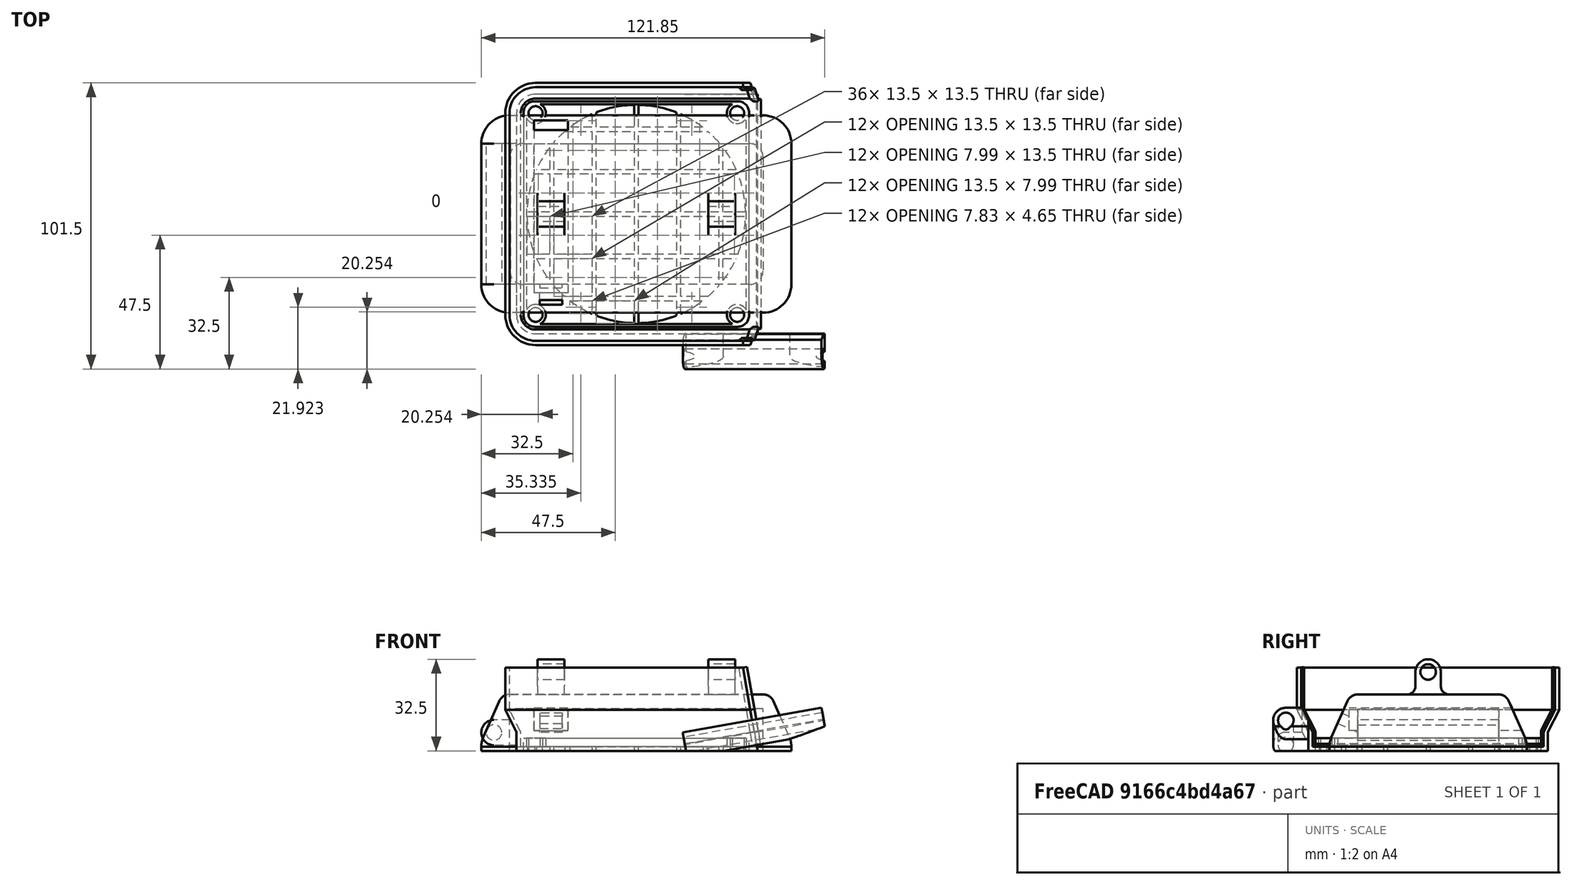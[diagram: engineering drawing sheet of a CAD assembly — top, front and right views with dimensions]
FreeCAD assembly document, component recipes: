
FREECAD ASSEMBLY — COMPONENT RECIPES ("Solder Fume Extractor 2x80mm fans - v2")

This assembly document has 5 components, labeled P0..P4 below (a component is one placed body or linked part). 5 of them carry a construction recipe — the FreeCAD feature program that regenerates the part from scratch, quoted from this document or its linked companion documents; the rest are supplied as boundary geometry only. No exploded tour is included for this assembly.
COMPONENT P0 — recipe-attached ("Fan1Holder", modeled in this document).
Construction recipe (the document's own serialized feature program — sketch geometry with constraints, then the solid features built on it; lengths are millimeters unless a unit is written):

FEATURE [Sketcher::SketchObject] Sketch
  ArcFitTolerance = 1e-06
  AttachmentSupport = -> [XY_Plane]
  FullyConstrained = true
  MakeInternals = false
  MapMode = 5
  sketch-geometry (13):
    g0: LineSegment StartX=-42.5 StartY=35.75 StartZ=0 EndX=-42.5 EndY=-35.75 EndZ=0
    g1: LineSegment StartX=-35.75 StartY=-42.5 StartZ=0 EndX=60 EndY=-42.5 EndZ=0
    g2: LineSegment StartX=60 StartY=-42.5 StartZ=0 EndX=60 EndY=42.5 EndZ=0
    g3: LineSegment StartX=60 StartY=42.5 StartZ=0 EndX=-35.75 EndY=42.5 EndZ=0
    g4: Circle CenterX=-35.75 CenterY=35.75 CenterZ=0 NormalX=0 NormalY=0 NormalZ=1 AngleXU=0 Radius=2.5
    g5: Circle CenterX=35.75 CenterY=35.75 CenterZ=0 NormalX=0 NormalY=0 NormalZ=1 AngleXU=0 Radius=2.5
    g6: Circle CenterX=-35.75 CenterY=-35.75 CenterZ=0 NormalX=0 NormalY=0 NormalZ=1 AngleXU=0 Radius=2.5
    g7: Circle CenterX=35.75 CenterY=-35.75 CenterZ=0 NormalX=0 NormalY=0 NormalZ=1 AngleXU=0 Radius=2.5
    g8: Circle CenterX=0 CenterY=0 CenterZ=0 NormalX=0 NormalY=0 NormalZ=1 AngleXU=0 Radius=38.75
    g9: ArcOfCircle CenterX=-35.75 CenterY=35.75 CenterZ=0 NormalX=0 NormalY=0 NormalZ=1 AngleXU=0 Radius=6.75 StartAngle=1.5708 EndAngle=3.14159
    g10: GeomPoint [constr] X=-42.5 Y=42.5 Z=0
    g11: ArcOfCircle CenterX=-35.75 CenterY=-35.75 CenterZ=0 NormalX=0 NormalY=0 NormalZ=1 AngleXU=0 Radius=6.75 StartAngle=3.14159 EndAngle=4.71239
    g12: GeomPoint [constr] X=-42.5 Y=-42.5 Z=0
  constraints (30):
    c: Coincident(g1,g2)
    c: Coincident(g2,g3)
    c: Vertical(g2)
    c: Horizontal(g1)
    c: Horizontal(g3)
    c: DistanceY(g12,g10) = 85
    c: Equal(g7,g5)
    c: Equal(g5,g4)
    c: Equal(g4,g6)
    c: Diameter(g7) = 5
    c: Symmetric(g7,g5,g-1)
    c: Symmetric(g5,g4,g-2)
    c: Vertical(g6,g4)
    c: Horizontal(g6,g7)
    c: DistanceX(g4,g5) = 71.5
    c: DistanceY(g6,g4) = 71.5
    c: Symmetric(g12,g10,g-1)
    c: Coincident(g8,g-1)
    c: Diameter(g8) = 77.5
    c: DistanceX(g10,g-1) = 42.5
    c: DistanceX(g1) = 60
    c: PointOnObject(g10,g0)
    c: PointOnObject(g10,g3)
    c: Tangent(g0,g9) = -1.5708
    c: Tangent(g3,g9) = -1.5708
    c: PointOnObject(g12,g1)
    c: Tangent(g0,g11) = -1.5708
    c: Tangent(g1,g11) = -1.5708
    c: Equal(g11,g9)
    c: Coincident(g9,g4)
FEATURE [PartDesign::Pad] Pad
  Direction = (0,0,1)
  Length = 1.5
  Length2 = 10
  Profile = -> Sketch
  ReferenceAxis = -> Sketch [N_Axis]
  Refine = true
  Suppressed = false
  Type = 0
FEATURE [Sketcher::SketchObject] Sketch001
  ArcFitTolerance = 1e-06
  AttachmentSupport = -> [Pad]
  ExternalGeometry = -> [Pad]
  FullyConstrained = true
  MakeInternals = false
  MapMode = 5
  Placement = pos=(0,0,1.5) rot=(0,0,1;0rad)
  sketch-geometry (12):
    g0: LineSegment StartX=60 StartY=42.5 StartZ=0 EndX=-35.75 EndY=42.5 EndZ=0
    g1: LineSegment StartX=-42.5 StartY=35.75 StartZ=0 EndX=-42.5 EndY=-35.75 EndZ=0
    g2: LineSegment StartX=-35.75 StartY=-42.5 StartZ=0 EndX=60 EndY=-42.5 EndZ=0
    g3: ArcOfCircle CenterX=-35.75 CenterY=-35.75 CenterZ=0 NormalX=0 NormalY=0 NormalZ=1 AngleXU=0 Radius=6.75 StartAngle=3.14159 EndAngle=4.71239
    g4: ArcOfCircle CenterX=-35.75 CenterY=35.75 CenterZ=0 NormalX=0 NormalY=0 NormalZ=1 AngleXU=0 Radius=6.75 StartAngle=1.5708 EndAngle=3.14159
    g5: LineSegment StartX=60 StartY=-42.5 StartZ=0 EndX=60 EndY=-41 EndZ=0
    g6: LineSegment StartX=60 StartY=-41 StartZ=0 EndX=-35.75 EndY=-41 EndZ=0
    g7: LineSegment StartX=-41 StartY=-35.75 StartZ=0 EndX=-41 EndY=35.75 EndZ=0
    g8: LineSegment StartX=-35.75 StartY=41 StartZ=0 EndX=60 EndY=41 EndZ=0
    g9: LineSegment StartX=60 StartY=41 StartZ=0 EndX=60 EndY=42.5 EndZ=0
    g10: ArcOfCircle CenterX=-35.75 CenterY=-35.75 CenterZ=0 NormalX=0 NormalY=0 NormalZ=1 AngleXU=0 Radius=5.25 StartAngle=3.14159 EndAngle=4.71239
    g11: ArcOfCircle CenterX=-35.75 CenterY=35.75 CenterZ=0 NormalX=0 NormalY=0 NormalZ=1 AngleXU=0 Radius=5.25 StartAngle=1.5708 EndAngle=3.14159
  constraints (30):
    c: Coincident(g0,g-3)
    c: Coincident(g0,g-4)
    c: Horizontal(g2)
    c: Symmetric(g2,g0,g-1)
    c: Equal(g2,g0)
    c: Coincident(g-5,g1)
    c: Coincident(g1,g-5)
    c: Coincident(g3,g2)
    c: Coincident(g3,g1)
    c: Coincident(g4,g1)
    c: Coincident(g4,g0)
    c: Equal(g4,g-4)
    c: Equal(g-4,g3)
    c: Coincident(g5,g2)
    c: Vertical(g5)
    c: Coincident(g6,g5)
    c: Horizontal(g6)
    c: Vertical(g7)
    c: Coincident(g9,g8)
    c: Coincident(g9,g0)
    c: Horizontal(g8)
    c: Vertical(g9)
    c: Equal(g5,g9)
    c: Equal(g6,g8)
    c: Tangent(g10,g6) = 1.5708
    c: Tangent(g10,g7) = 1.5708
    c: Tangent(g11,g7) = 1.5708
    c: Tangent(g11,g8) = 1.5708
    c: DistanceY(g5,g5) = 1.5
    c: Coincident(g11,g4)
FEATURE [PartDesign::Pad] Pad001
  BaseFeature = -> Pad
  Direction = (0,0,1)
  Length = 5
  Length2 = 10
  Profile = -> Sketch001
  ReferenceAxis = -> Sketch001 [N_Axis]
  Refine = true
  Suppressed = false
  Type = 0
FEATURE [Sketcher::SketchObject] Sketch002
  ArcFitTolerance = 1e-06
  AttachmentSupport = -> [Pad001]
  ExternalGeometry = -> [Pad001]
  FullyConstrained = true
  MakeInternals = false
  MapMode = 5
  Placement = pos=(60,0,0) rot=(0.57735,0.57735,0.57735;2.0944rad)
  sketch-geometry (9):
    g0: LineSegment StartX=41.1112 StartY=6.9583 StartZ=0 EndX=45 EndY=14.5 EndZ=0
    g1: LineSegment [constr] StartX=45 StartY=14.5 StartZ=0 EndX=46.5 EndY=14.5 EndZ=0
    g2: LineSegment StartX=46.5 StartY=14.5 StartZ=0 EndX=42.6112 EndY=6.9583 EndZ=0
    g3: ArcOfCircle CenterX=43.5 CenterY=6.5 CenterZ=0 NormalX=0 NormalY=0 NormalZ=1 AngleXU=0 Radius=1 StartAngle=2.66551 EndAngle=3.14159
    g4: ArcOfCircle CenterX=42 CenterY=6.5 CenterZ=0 NormalX=0 NormalY=0 NormalZ=1 AngleXU=0 Radius=1 StartAngle=2.66551 EndAngle=3.14159
    g5: LineSegment StartX=42.5 StartY=6.5 StartZ=0 EndX=41 EndY=6.5 EndZ=0
    g6: LineSegment StartX=45 StartY=14.5 StartZ=0 EndX=45 EndY=29.5 EndZ=0
    g7: LineSegment StartX=45 StartY=29.5 StartZ=0 EndX=46.5 EndY=29.5 EndZ=0
    g8: LineSegment StartX=46.5 StartY=29.5 StartZ=0 EndX=46.5 EndY=14.5 EndZ=0
  constraints (24):
    c: Coincident(g0,g1)
    c: Horizontal(g1)
    c: Coincident(g1,g2)
    c: Coincident(g3,g-3)
    c: Coincident(g4,g-3)
    c: Tangent(g4,g0) = 1.5708
    c: Tangent(g3,g2) = -1.5708
    c: Coincident(g5,g3)
    c: Coincident(g5,g4)
    c: Perpendicular(g3,g5)
    c: Perpendicular(g4,g5)
    c: Equal(g1,g5)
    c: Radius(g4) = 1
    c: DistanceY(g3,g1) = 8
    c: DistanceX(g3,g1) = 4
    c: Equal(g4,g3)
    c: Coincident(g0,g6)
    c: Vertical(g6)
    c: Coincident(g6,g7)
    c: Coincident(g7,g8)
    c: Coincident(g8,g1)
    c: Vertical(g8)
    c: Horizontal(g7)
    c: DistanceY(g8,g8) = 15
FEATURE [PartDesign::AdditivePipe] AdditivePipe
  AuxilleryCurvelinear = true
  AuxillerySpineTangent = false
  BaseFeature = -> Pad001
  Binormal = (0,0,0)
  Mode = 0
  Profile = -> Sketch002
  Refine = true
  Spine = -> Pad001 [Edge32,Edge33,Edge34,Edge35,Edge36]
  SpineTangent = false
  Suppressed = false
  Transformation = 0
  Transition = 0
FEATURE [Sketcher::SketchObject] Sketch003
  ArcFitTolerance = 1e-06
  AttachmentSupport = -> [XY_Plane]
  ExternalGeometry = -> [AdditivePipe]
  FullyConstrained = true
  MakeInternals = false
  MapMode = 5
  sketch-geometry (5):
    g0: LineSegment StartX=-30.75 StartY=42.5 StartZ=0 EndX=-30.75 EndY=-42.5 EndZ=0
    g1: LineSegment StartX=-30.75 StartY=-42.5 StartZ=0 EndX=-29.25 EndY=-42.5 EndZ=0
    g2: LineSegment StartX=-29.25 StartY=-42.5 StartZ=0 EndX=-29.25 EndY=42.5 EndZ=0
    g3: LineSegment StartX=-29.25 StartY=42.5 StartZ=0 EndX=-30.75 EndY=42.5 EndZ=0
    g4: GeomPoint [constr] X=-30 Y=0 Z=0
  constraints (13):
    c: Coincident(g0,g1)
    c: Coincident(g1,g2)
    c: Coincident(g2,g3)
    c: Coincident(g3,g0)
    c: Vertical(g0)
    c: Vertical(g2)
    c: Horizontal(g1)
    c: Horizontal(g3)
    c: Symmetric(g2,g0,g4)
    c: PointOnObject(g4,g-1)
    c: PointOnObject(g1,g-3)
    c: DistanceX(g3,g3) = 1.5
    c: DistanceX(g4,g-1) = 30
FEATURE [PartDesign::Pad] Pad002
  BaseFeature = -> AdditivePipe
  Direction = (0,0,1)
  Length = 10
  Length2 = 10
  Profile = -> Sketch003
  ReferenceAxis = -> Sketch003 [N_Axis]
  Refine = true
  Suppressed = false
  Type = 3
  UpToFace = -> AdditivePipe [Face4]
FEATURE [PartDesign::LinearPattern] LinearPattern
  BaseFeature = -> Pad002
  Direction = -> Sketch003 [H_Axis]
  Length = 60
  Mode = 0
  Occurrences = 5
  Offset = 15
  Originals = -> [Pad002]
  Refine = true
  Suppressed = false
  TransformMode = 0
FEATURE [Sketcher::SketchObject] Sketch004
  ArcFitTolerance = 1e-06
  AttachmentSupport = -> [XY_Plane]
  ExternalGeometry = -> [LinearPattern]
  FullyConstrained = true
  MakeInternals = false
  MapMode = 5
  sketch-geometry (5):
    g0: LineSegment StartX=42.5 StartY=29.25 StartZ=0 EndX=42.5 EndY=30.75 EndZ=0
    g1: LineSegment StartX=42.5 StartY=30.75 StartZ=0 EndX=-42.5 EndY=30.75 EndZ=0
    g2: LineSegment StartX=-42.5 StartY=30.75 StartZ=0 EndX=-42.5 EndY=29.25 EndZ=0
    g3: LineSegment StartX=-42.5 StartY=29.25 StartZ=0 EndX=42.5 EndY=29.25 EndZ=0
    g4: GeomPoint [constr] X=0 Y=30 Z=0
  constraints (13):
    c: Coincident(g0,g1)
    c: Coincident(g1,g2)
    c: Coincident(g2,g3)
    c: Coincident(g3,g0)
    c: Vertical(g0)
    c: Vertical(g2)
    c: Horizontal(g1)
    c: Horizontal(g3)
    c: Symmetric(g2,g0,g4)
    c: PointOnObject(g4,g-2)
    c: PointOnObject(g1,g-3)
    c: DistanceY(g4) = 30
    c: DistanceY(g0,g0) = 1.5
FEATURE [PartDesign::Pad] Pad003
  BaseFeature = -> LinearPattern
  Direction = (0,0,1)
  Length = 10
  Length2 = 10
  Profile = -> Sketch004
  ReferenceAxis = -> Sketch004 [N_Axis]
  Refine = true
  Suppressed = false
  Type = 3
  UpToFace = -> LinearPattern [Face68]
FEATURE [PartDesign::LinearPattern] LinearPattern001
  BaseFeature = -> Pad003
  Direction = -> Sketch004 [V_Axis]
  Length = 60
  Mode = 0
  Occurrences = 5
  Offset = 15
  Originals = -> [Pad003]
  Refine = true
  Reversed = true
  Suppressed = false
  TransformMode = 0
FEATURE [PartDesign::CoordinateSystem] FanMountHole
  AttacherType = Attacher::AttachEngine3D
  AttachmentSupport = -> [LinearPattern001]
  MapMode = 11
  Placement = pos=(-35.75,-35.75,0) rot=(0,0,1;1.5708rad)
FEATURE [Sketcher::SketchObject] Sketch005
  ArcFitTolerance = 1e-06
  AttachmentSupport = -> [XZ_Plane]
  ExternalGeometry = -> [LinearPattern001]
  FullyConstrained = true
  MakeInternals = false
  MapMode = 5
  Placement = pos=(0,0,0) rot=(1,0,0;1.5708rad)
  sketch-geometry (4):
    g0: LineSegment StartX=60 StartY=29.5 StartZ=0 EndX=60 EndY=0 EndZ=0
    g1: LineSegment StartX=60 StartY=0 StartZ=0 EndX=43 EndY=0 EndZ=0
    g2: LineSegment StartX=43 StartY=0 StartZ=0 EndX=37.7984 EndY=29.5 EndZ=0
    g3: LineSegment StartX=37.7984 StartY=29.5 StartZ=0 EndX=60 EndY=29.5 EndZ=0
  constraints (11):
    c: PointOnObject(g0,g-1)
    c: Vertical(g0)
    c: Coincident(g0,g1)
    c: PointOnObject(g1,g-1)
    c: Coincident(g1,g2)
    c: Coincident(g2,g3)
    c: Coincident(g3,g0)
    c: DistanceX(g-1,g1) = 43
    c: Angle(g1,g2) = 1.74533
    c: Coincident(g0,g-3)
    c: PointOnObject(g2,g-3)
FEATURE [PartDesign::Pocket] Pocket
  BaseFeature = -> LinearPattern001
  Direction = (0,1,-2e-16)
  Length = 5
  Length2 = 5
  Midplane = true
  Profile = -> Sketch005
  ReferenceAxis = -> Sketch005 [N_Axis]
  Refine = true
  Suppressed = false
  Type = 1
FEATURE [PartDesign::CoordinateSystem] OtherFanHolder
  AttacherType = Attacher::AttachEngine3D
  AttachmentSupport = -> [Pocket]
  MapMode = 45
  Placement = pos=(42.8701,0,0.736527) rot=(0.642788,0,0.766044;3.14159rad)
FEATURE [PartDesign::CoordinateSystem] FilterHolderMount
  AttacherType = Attacher::AttachEngine3D
  AttachmentSupport = -> [Pocket]
  MapMode = 11
  Placement = pos=(-35.75,35.75,1.5) rot=(0,0,1;1.5708rad)
FEATURE [Sketcher::SketchObject] Sketch010
  ArcFitTolerance = 1e-06
  AttachmentSupport = -> [XZ_Plane]
  ExternalGeometry = -> [Pocket]
  FullyConstrained = true
  MakeInternals = false
  MapMode = 5
  Placement = pos=(0,0,0) rot=(1,0,0;1.5708rad)
  sketch-geometry (7):
    g0: ArcOfCircle CenterX=-43.5 CenterY=6.5 CenterZ=0 NormalX=0 NormalY=0 NormalZ=1 AngleXU=0 Radius=1 StartAngle=-2.4e-14 EndAngle=0.476081
    g1: LineSegment StartX=-42.5 StartY=6.5 StartZ=0 EndX=-42.5 EndY=2 EndZ=0
    g2: LineSegment StartX=-42.5 StartY=2 StartZ=0 EndX=-50.5 EndY=2 EndZ=0
    g3: LineSegment StartX=-42.6112 StartY=6.9583 StartZ=0 EndX=-44.6953 EndY=11 EndZ=0
    g4: LineSegment StartX=-44.6953 StartY=11 StartZ=0 EndX=-50.5 EndY=11 EndZ=0
    g5: ArcOfCircle CenterX=-50.5 CenterY=6.5 CenterZ=0 NormalX=0 NormalY=0 NormalZ=1 AngleXU=0 Radius=4.5 StartAngle=1.5708 EndAngle=4.71239
    g6: Circle CenterX=-50.5 CenterY=6.5 CenterZ=0 NormalX=0 NormalY=0 NormalZ=1 AngleXU=0 Radius=2.75
  constraints (18):
    c: Coincident(g0,g-5)
    c: Coincident(g0,g-5)
    c: Equal(g-5,g0)
    c: Coincident(g1,g0)
    c: PointOnObject(g1,g-3)
    c: Coincident(g2,g1)
    c: Horizontal(g2)
    c: Coincident(g3,g0)
    c: PointOnObject(g3,g-4)
    c: Horizontal(g4)
    c: Tangent(g5,g4) = -1.5708
    c: Tangent(g5,g2) = 1.5708
    c: Diameter(g5) = 9
    c: Diameter(g6) = 5.5
    c: Coincident(g6,g5)
    c: Horizontal(g0,g5)
    c: Coincident(g3,g4)
    c: DistanceX(g5,g-4) = 4
FEATURE [PartDesign::Pad] Pad008
  BaseFeature = -> Pocket
  Direction = (0,-1,2e-16)
  Length = 50
  Length2 = 10
  Midplane = true
  Profile = -> Sketch010
  ReferenceAxis = -> Sketch010 [N_Axis]
  Refine = true
  Suppressed = false
  Type = 0
FEATURE [Sketcher::SketchObject] Sketch011
  ArcFitTolerance = 1e-06
  AttachmentSupport = -> [Pad008]
  ExternalGeometry = -> [Pad008]
  FullyConstrained = true
  MakeInternals = false
  MapMode = 5
  Placement = pos=(41.7034,1.6e-15,7.35343) rot=(0.540716,0.540716,0.6444;1.99673rad)
  sketch-geometry (7):
    g0: ArcOfCircle CenterX=-43.0908 CenterY=-0.761797 CenterZ=0 NormalX=0 NormalY=0 NormalZ=1 AngleXU=0 Radius=0.6 StartAngle=6.10761 EndAngle=6.92787
    g1: LineSegment StartX=-44.66 StartY=3.6334 StartZ=0 EndX=-42.6112 EndY=-0.401229 EndZ=0
    g2: LineSegment StartX=-42.5 StartY=-5.3666 StartZ=0 EndX=-42.5 EndY=-0.866599 EndZ=0
    g3: LineSegment StartX=-42.5 StartY=-5.3666 StartZ=0 EndX=-50.5 EndY=-5.3666 EndZ=0
    g4: LineSegment StartX=-44.66 StartY=3.6334 StartZ=0 EndX=-50.5 EndY=3.6334 EndZ=0
    g5: ArcOfCircle CenterX=-50.5 CenterY=-0.866599 CenterZ=0 NormalX=0 NormalY=0 NormalZ=1 AngleXU=0 Radius=4.5 StartAngle=1.5708 EndAngle=4.71239
    g6: Circle CenterX=-50.5 CenterY=-0.866599 CenterZ=0 NormalX=0 NormalY=0 NormalZ=1 AngleXU=0 Radius=2.75
  constraints (18):
    c: Coincident(g0,g-3)
    c: Coincident(g0,g-4)
    c: Radius(g0) = 0.6
    c: Coincident(g3,g2)
    c: Horizontal(g3)
    c: Coincident(g4,g1)
    c: Horizontal(g4)
    c: Tangent(g5,g4) = -1.5708
    c: Tangent(g5,g3) = 1.5708
    c: Diameter(g5) = 9
    c: Horizontal(g5,g2)
    c: Coincident(g6,g5)
    c: Diameter(g6) = 5.5
    c: DistanceX(g5,g-4) = 4
    c: Coincident(g2,g0)
    c: PointOnObject(g1,g-4)
    c: PointOnObject(g2,g-3)
    c: Coincident(g0,g1)
FEATURE [PartDesign::Pad] Pad009
  BaseFeature = -> Pad008
  Direction = (0.984808,-1e-16,0.173648)
  Length = 50
  Length2 = 10
  Midplane = true
  Profile = -> Sketch011
  ReferenceAxis = -> Sketch011 [N_Axis]
  Refine = true
  Suppressed = false
  Type = 0
FEATURE [Sketcher::SketchObject] Sketch031
  ArcFitTolerance = 1e-06
  AttachmentSupport = -> [XZ_Plane]
  FullyConstrained = true
  MakeInternals = false
  MapMode = 5
  Placement = pos=(0,0,0) rot=(1,0,0;1.5708rad)
  sketch-geometry (8):
    g0: LineSegment StartX=0 StartY=0 StartZ=0 EndX=0 EndY=-5 EndZ=0
    g1: LineSegment StartX=0 StartY=-5 StartZ=0 EndX=43 EndY=-5 EndZ=0
    g2: LineSegment StartX=43 StartY=-5 StartZ=0 EndX=43 EndY=1.24e-14 EndZ=0
    g3: LineSegment StartX=43 StartY=1.24e-14 StartZ=0 EndX=0 EndY=0 EndZ=0
    g4: LineSegment StartX=43 StartY=1.24e-14 StartZ=0 EndX=44.7101 EndY=-4.69846 EndZ=0
    g5: LineSegment StartX=44.7101 StartY=-4.69846 StartZ=0 EndX=85.1169 EndY=10.0084 EndZ=0
    g6: LineSegment StartX=85.1169 StartY=10.0084 StartZ=0 EndX=83.4068 EndY=14.7069 EndZ=0
    g7: LineSegment StartX=83.4068 StartY=14.7069 StartZ=0 EndX=43 EndY=1.24e-14 EndZ=0
  constraints (22):
    c: Angle(g-3,g-1) = 1.39626
    c: Coincident(g0,g1)
    c: Coincident(g1,g2)
    c: Coincident(g2,g3)
    c: Coincident(g3,g0)
    c: Vertical(g0)
    c: Vertical(g2)
    c: Horizontal(g1)
    c: Coincident(g0,g-1)
    c: Coincident(g2,g-3)
    c: DistanceY(g2,g2) = 5
    c: Coincident(g2,g4)
    c: Coincident(g4,g5)
    c: Coincident(g5,g6)
    c: Coincident(g6,g7)
    c: Coincident(g7,g4)
    c: Perpendicular(g7,g4)
    c: Perpendicular(g6,g7)
    c: Equal(g4,g6)
    c: Equal(g6,g2)
    c: Equal(g7,g1)
    c: Angle(g7,g-3) = 1.39626
FEATURE [PartDesign::Pocket] Pocket008
  BaseFeature = -> Pad009
  Direction = (0,1,-2e-16)
  Length = 5
  Length2 = 5
  Profile = -> Sketch031
  ReferenceAxis = -> Sketch031 [N_Axis]
  Refine = true
  Reversed = true
  Suppressed = false
  Type = 1
FEATURE [PartDesign::CoordinateSystem] Mount1
  AttacherType = Attacher::AttachEngine3D
  AttachmentSupport = -> [Pocket008]
  MapMode = 45
  Placement = pos=(-50.5,-7e-16,6.5) rot=(0,0.707107,0.707107;3.14159rad)
FEATURE [PartDesign::CoordinateSystem] Mount2
  AttacherType = Attacher::AttachEngine3D
  AttachmentOffset = pos=(0,0,25) rot=(0,0,1;0rad)
  AttachmentSupport = -> [Pocket008]
  MapMode = 11
  Placement = pos=(41.8539,-50.5,6.5) rot=(0.642788,0,0.766044;3.14159rad)
FEATURE [Sketcher::SketchObject] Sketch032
  ArcFitTolerance = 1e-06
  AttachmentSupport = -> [XZ_Plane]
  ExternalGeometry = -> [Pocket008]
  FullyConstrained = true
  MakeInternals = false
  MapMode = 5
  Placement = pos=(0,0,0) rot=(1,0,0;1.5708rad)
  sketch-geometry (7):
    g0: LineSegment StartX=41.2355 StartY=1.5 StartZ=0 EndX=42.7355 EndY=1.5 EndZ=0
    g1: LineSegment StartX=42.7355 StartY=1.5 StartZ=0 EndX=44.145 EndY=2.01303 EndZ=0
    g2: ArcOfCircle CenterX=41.2355 CenterY=2.10733 CenterZ=0 NormalX=0 NormalY=0 NormalZ=1 AngleXU=0 Radius=0.607328 StartAngle=4.71239 EndAngle=6.06406
    g3: ArcOfCircle CenterX=43.9373 CenterY=2.58373 CenterZ=0 NormalX=0 NormalY=0 NormalZ=1 AngleXU=0 Radius=0.607328 StartAngle=3.70978 EndAngle=5.06145
    g4: LineSegment StartX=42.3157 StartY=2.4414 StartZ=0 EndX=42.8081 EndY=2.52822 EndZ=0
    g5: ArcOfCircle CenterX=42.4211 CenterY=1.84329 CenterZ=0 NormalX=0 NormalY=0 NormalZ=1 AngleXU=0 Radius=0.607328 StartAngle=1.74533 EndAngle=2.92247
    g6: ArcOfCircle CenterX=42.9135 CenterY=1.93012 CenterZ=0 NormalX=0 NormalY=0 NormalZ=1 AngleXU=0 Radius=0.607328 StartAngle=0.568188 EndAngle=1.74533
  constraints (17):
    c: Coincident(g0,g-4)
    c: Horizontal(g0)
    c: Coincident(g0,g1)
    c: DistanceX(g0,g0) = 1.5
    c: Angle(g1,g-4) = 1.39626
    c: Symmetric(g4,g4,g-4)
    c: Tangent(g5,g4) = 1.5708
    c: Tangent(g5,g2) = 1.5708
    c: Tangent(g6,g4) = 1.5708
    c: Tangent(g6,g3) = 1.5708
    c: Tangent(g3,g1) = -1.5708
    c: Tangent(g2,g0) = -1.5708
    c: Equal(g2,g5)
    c: Equal(g5,g6)
    c: Equal(g6,g3)
    c: Distance(g0,g4) = 1
    c: Distance(g4) = 0.5
FEATURE [PartDesign::AdditivePipe] AdditivePipe002
  AuxilleryCurvelinear = true
  AuxillerySpineTangent = false
  BaseFeature = -> Pocket008
  Binormal = (0,0,0)
  Mode = 0
  Profile = -> Sketch032
  Refine = true
  Spine = -> Pocket008 [Edge31,Edge30,Edge29,Edge28,Edge32,Edge33,Edge34,Edge35,Edge27]
  SpineTangent = false
  Suppressed = false
  Transformation = 0
  Transition = 1
FEATURE [PartDesign::Body] Body  label="Fan1Holder"
  AllowCompound = false
  Group = -> [Sketch,Pad,Sketch001,Pad001,Sketch002,AdditivePipe,Sketch003,Pad002,LinearPattern,Sketch004,Pad003,LinearPattern001,FanMountHole,Sketch005,Pocket,OtherFanHolder,FilterHolderMount,Sketch010,Pad008,Sketch011,Pad009,Mount1,Mount2,Sketch031,Pocket008,Sketch032,AdditivePipe002]
  Origin = -> Origin
  Tip = -> AdditivePipe002
COMPONENT P1 — recipe-attached ("FilterHolder", modeled in this document).
Construction recipe (the document's own serialized feature program — sketch geometry with constraints, then the solid features built on it; lengths are millimeters unless a unit is written):

FEATURE [Sketcher::SketchObject] Sketch006
  ArcFitTolerance = 1e-06
  AttachmentSupport = -> [XY_Plane002]
  FullyConstrained = true
  MakeInternals = false
  MapMode = 5
  sketch-geometry (15):
    g0: LineSegment StartX=40 StartY=-36 StartZ=0 EndX=40 EndY=36 EndZ=0
    g1: LineSegment StartX=36 StartY=40 StartZ=0 EndX=-36 EndY=40 EndZ=0
    g2: LineSegment StartX=-40 StartY=36 StartZ=0 EndX=-40 EndY=-36 EndZ=0
    g3: LineSegment StartX=-36 StartY=-40 StartZ=0 EndX=36 EndY=-40 EndZ=0
    g4: ArcOfCircle CenterX=36 CenterY=-36 CenterZ=0 NormalX=0 NormalY=0 NormalZ=1 AngleXU=0 Radius=4 StartAngle=4.71239 EndAngle=6.28319
    g5: ArcOfCircle CenterX=36 CenterY=36 CenterZ=0 NormalX=0 NormalY=0 NormalZ=1 AngleXU=0 Radius=4 StartAngle=2e-16 EndAngle=1.5708
    g6: ArcOfCircle CenterX=-36 CenterY=36 CenterZ=0 NormalX=0 NormalY=0 NormalZ=1 AngleXU=0 Radius=4 StartAngle=1.5708 EndAngle=3.14159
    g7: ArcOfCircle CenterX=-36 CenterY=-36 CenterZ=0 NormalX=0 NormalY=0 NormalZ=1 AngleXU=0 Radius=4 StartAngle=3.14159 EndAngle=4.71239
    g8: GeomPoint [constr] X=40 Y=-40 Z=0
    g9: GeomPoint [constr] X=-40 Y=40 Z=0
    g10: Circle CenterX=-35.75 CenterY=35.75 CenterZ=0 NormalX=0 NormalY=0 NormalZ=1 AngleXU=0 Radius=2.5
    g11: Circle CenterX=35.75 CenterY=35.75 CenterZ=0 NormalX=0 NormalY=0 NormalZ=1 AngleXU=0 Radius=2.5
    g12: Circle CenterX=35.75 CenterY=-35.75 CenterZ=0 NormalX=0 NormalY=0 NormalZ=1 AngleXU=0 Radius=2.5
    g13: Circle CenterX=-35.75 CenterY=-35.75 CenterZ=0 NormalX=0 NormalY=0 NormalZ=1 AngleXU=0 Radius=2.5
    g14: Circle CenterX=0 CenterY=0 CenterZ=0 NormalX=0 NormalY=0 NormalZ=1 AngleXU=0 Radius=38.75
  constraints (34):
    c: Tangent(g0,g4) = -1.5708
    c: Tangent(g0,g5) = -1.5708
    c: Tangent(g1,g5) = -1.5708
    c: Tangent(g1,g6) = -1.5708
    c: Tangent(g2,g6) = -1.5708
    c: Tangent(g2,g7) = -1.5708
    c: Tangent(g3,g7) = -1.5708
    c: Tangent(g3,g4) = -1.5708
    c: Vertical(g2)
    c: Horizontal(g1)
    c: Equal(g4,g5)
    c: Equal(g5,g6)
    c: Equal(g6,g7)
    c: PointOnObject(g8,g0)
    c: PointOnObject(g8,g3)
    c: PointOnObject(g9,g1)
    c: PointOnObject(g9,g2)
    c: Radius(g7) = 4
    c: Symmetric(g3,g3,g-2)
    c: Symmetric(g0,g0,g-1)
    c: Equal(g0,g3)
    c: DistanceY(g3,g1) = 80
    c: Equal(g10,g11)
    c: Equal(g11,g12)
    c: Equal(g12,g13)
    c: Symmetric(g10,g11,g-2)
    c: Symmetric(g11,g12,g-1)
    c: Horizontal(g12,g13)
    c: Vertical(g13,g10)
    c: DistanceY(g13,g10) = 71.5
    c: DistanceX(g10,g11) = 71.5
    c: Diameter(g11) = 5
    c: Coincident(g14,g-1)
    c: Diameter(g14) = 77.5
FEATURE [PartDesign::Pad] Pad004
  Direction = (0,0,1)
  Length = 1.5
  Length2 = 10
  Profile = -> Sketch006
  ReferenceAxis = -> Sketch006 [N_Axis]
  Refine = true
  Suppressed = false
  Type = 0
FEATURE [Sketcher::SketchObject] Sketch007
  ArcFitTolerance = 1e-06
  AttachmentSupport = -> [XY_Plane002]
  ExternalGeometry = -> [Pad004]
  FullyConstrained = true
  MakeInternals = false
  MapMode = 5
  sketch-geometry (5):
    g0: LineSegment StartX=-29.25 StartY=-40 StartZ=0 EndX=-29.25 EndY=40 EndZ=0
    g1: LineSegment StartX=-29.25 StartY=40 StartZ=0 EndX=-30.75 EndY=40 EndZ=0
    g2: LineSegment StartX=-30.75 StartY=40 StartZ=0 EndX=-30.75 EndY=-40 EndZ=0
    g3: LineSegment StartX=-30.75 StartY=-40 StartZ=0 EndX=-29.25 EndY=-40 EndZ=0
    g4: GeomPoint [constr] X=-30 Y=0 Z=0
  constraints (13):
    c: Coincident(g0,g1)
    c: Coincident(g1,g2)
    c: Coincident(g2,g3)
    c: Coincident(g3,g0)
    c: Vertical(g0)
    c: Vertical(g2)
    c: Horizontal(g1)
    c: Horizontal(g3)
    c: Symmetric(g2,g0,g4)
    c: PointOnObject(g4,g-1)
    c: PointOnObject(g1,g-3)
    c: DistanceX(g4,g-1) = 30
    c: DistanceX(g1,g1) = 1.5
FEATURE [PartDesign::Pad] Pad005
  BaseFeature = -> Pad004
  Direction = (0,0,1)
  Length = 10
  Length2 = 10
  Profile = -> Sketch007
  ReferenceAxis = -> Sketch007 [N_Axis]
  Refine = true
  Suppressed = false
  Type = 3
  UpToFace = -> Pad004 [Face15]
FEATURE [PartDesign::LinearPattern] LinearPattern002
  BaseFeature = -> Pad005
  Direction = -> Sketch007 [H_Axis]
  Length = 60
  Mode = 0
  Occurrences = 5
  Offset = 15
  Originals = -> [Pad005]
  Refine = true
  Suppressed = false
  TransformMode = 0
FEATURE [Sketcher::SketchObject] Sketch008
  ArcFitTolerance = 1e-06
  AttachmentSupport = -> [XY_Plane002]
  ExternalGeometry = -> [LinearPattern002]
  FullyConstrained = true
  MakeInternals = false
  MapMode = 5
  sketch-geometry (5):
    g0: LineSegment StartX=40 StartY=-30.75 StartZ=0 EndX=40 EndY=-29.25 EndZ=0
    g1: LineSegment StartX=40 StartY=-29.25 StartZ=0 EndX=-40 EndY=-29.25 EndZ=0
    g2: LineSegment StartX=-40 StartY=-29.25 StartZ=0 EndX=-40 EndY=-30.75 EndZ=0
    g3: LineSegment StartX=-40 StartY=-30.75 StartZ=0 EndX=40 EndY=-30.75 EndZ=0
    g4: GeomPoint [constr] X=0 Y=-30 Z=0
  constraints (13):
    c: Coincident(g0,g1)
    c: Coincident(g1,g2)
    c: Coincident(g2,g3)
    c: Coincident(g3,g0)
    c: Vertical(g0)
    c: Vertical(g2)
    c: Horizontal(g1)
    c: Horizontal(g3)
    c: Symmetric(g2,g0,g4)
    c: PointOnObject(g4,g-2)
    c: PointOnObject(g1,g-3)
    c: DistanceY(g4,g-1) = 30
    c: DistanceY(g0,g0) = 1.5
FEATURE [PartDesign::Pad] Pad006
  BaseFeature = -> LinearPattern002
  Direction = (0,0,1)
  Length = 10
  Length2 = 10
  Profile = -> Sketch008
  ReferenceAxis = -> Sketch008 [N_Axis]
  Refine = true
  Suppressed = false
  Type = 3
  UpToFace = -> LinearPattern002 [Face32]
FEATURE [PartDesign::LinearPattern] LinearPattern003
  BaseFeature = -> Pad006
  Direction = -> Sketch008 [V_Axis]
  Length = 60
  Mode = 0
  Occurrences = 5
  Offset = 15
  Originals = -> [Pad006]
  Refine = true
  Suppressed = false
  TransformMode = 0
FEATURE [Sketcher::SketchObject] Sketch009
  ArcFitTolerance = 1e-06
  AttachmentSupport = -> [LinearPattern003]
  ExternalGeometry = -> [LinearPattern003]
  FullyConstrained = true
  MakeInternals = false
  MapMode = 5
  Placement = pos=(0,0,1.5) rot=(0,0,1;0rad)
  sketch-geometry (20):
    g0: LineSegment StartX=-40 StartY=36 StartZ=0 EndX=-40 EndY=-36 EndZ=0
    g1: LineSegment StartX=-36 StartY=-40 StartZ=0 EndX=36 EndY=-40 EndZ=0
    g2: LineSegment StartX=40 StartY=-36 StartZ=0 EndX=40 EndY=36 EndZ=0
    g3: LineSegment StartX=36 StartY=40 StartZ=0 EndX=-36 EndY=40 EndZ=0
    g4: ArcOfCircle CenterX=-36 CenterY=36 CenterZ=0 NormalX=0 NormalY=0 NormalZ=1 AngleXU=0 Radius=4 StartAngle=1.5708 EndAngle=3.14159
    g5: ArcOfCircle CenterX=-36 CenterY=-36 CenterZ=0 NormalX=0 NormalY=0 NormalZ=1 AngleXU=0 Radius=4 StartAngle=3.14159 EndAngle=4.71239
    g6: ArcOfCircle CenterX=36 CenterY=-36 CenterZ=0 NormalX=0 NormalY=0 NormalZ=1 AngleXU=0 Radius=4 StartAngle=4.71239 EndAngle=6.28319
    g7: ArcOfCircle CenterX=36 CenterY=36 CenterZ=0 NormalX=0 NormalY=0 NormalZ=1 AngleXU=0 Radius=4 StartAngle=-9e-16 EndAngle=1.5708
    g8: GeomPoint [constr] X=-40 Y=40 Z=0
    g9: GeomPoint [constr] X=40 Y=-40 Z=0
    g10: LineSegment StartX=-39 StartY=36 StartZ=0 EndX=-39 EndY=-36 EndZ=0
    g11: LineSegment StartX=-36 StartY=-39 StartZ=0 EndX=36 EndY=-39 EndZ=0
    g12: LineSegment StartX=39 StartY=-36 StartZ=0 EndX=39 EndY=36 EndZ=0
    g13: LineSegment StartX=36 StartY=39 StartZ=0 EndX=-36 EndY=39 EndZ=0
    g14: ArcOfCircle CenterX=-36 CenterY=36 CenterZ=0 NormalX=0 NormalY=0 NormalZ=1 AngleXU=0 Radius=3 StartAngle=1.5708 EndAngle=3.14159
    g15: ArcOfCircle CenterX=-36 CenterY=-36 CenterZ=0 NormalX=0 NormalY=0 NormalZ=1 AngleXU=0 Radius=3 StartAngle=3.14159 EndAngle=4.71239
    g16: ArcOfCircle CenterX=36 CenterY=-36 CenterZ=0 NormalX=0 NormalY=0 NormalZ=1 AngleXU=0 Radius=3 StartAngle=4.71239 EndAngle=6.28319
    g17: ArcOfCircle CenterX=36 CenterY=36 CenterZ=0 NormalX=0 NormalY=0 NormalZ=1 AngleXU=0 Radius=3 StartAngle=-9e-16 EndAngle=1.5708
    g18: GeomPoint [constr] X=-39 Y=39 Z=0
    g19: GeomPoint [constr] X=39 Y=-39 Z=0
  constraints (44):
    c: Tangent(g0,g4) = -1.5708
    c: Tangent(g0,g5) = -1.5708
    c: Tangent(g1,g5) = -1.5708
    c: Tangent(g1,g6) = -1.5708
    c: Tangent(g2,g6) = -1.5708
    c: Tangent(g2,g7) = -1.5708
    c: Tangent(g3,g7) = -1.5708
    c: Tangent(g3,g4) = -1.5708
    c: Vertical(g0)
    c: Vertical(g2)
    c: Horizontal(g1)
    c: Equal(g4,g5)
    c: Equal(g5,g6)
    c: Equal(g6,g7)
    c: PointOnObject(g8,g0)
    c: PointOnObject(g8,g3)
    c: PointOnObject(g9,g1)
    c: PointOnObject(g9,g2)
    c: Coincident(g3,g-5)
    c: Equal(g-5,g7)
    c: Coincident(g3,g-3)
    c: Equal(g3,g2)
    c: Tangent(g10,g14) = -1.5708
    c: Tangent(g10,g15) = -1.5708
    c: Tangent(g11,g15) = -1.5708
    c: Tangent(g11,g16) = -1.5708
    c: Tangent(g12,g16) = -1.5708
    c: Tangent(g12,g17) = -1.5708
    c: Tangent(g13,g17) = -1.5708
    c: Tangent(g13,g14) = -1.5708
    c: Vertical(g10)
    c: Horizontal(g11)
    c: Equal(g14,g15)
    c: Equal(g15,g16)
    c: Equal(g16,g17)
    c: PointOnObject(g18,g10)
    c: PointOnObject(g18,g13)
    c: PointOnObject(g19,g11)
    c: PointOnObject(g19,g12)
    c: Symmetric(g12,g12,g-1)
    c: Symmetric(g13,g13,g-2)
    c: Equal(g11,g12)
    c: DistanceX(g12,g2) = 1
    c: Horizontal(g2,g12)
FEATURE [PartDesign::Pad] Pad007
  BaseFeature = -> LinearPattern003
  Direction = (0,0,1)
  Length = 3
  Length2 = 10
  Profile = -> Sketch009
  ReferenceAxis = -> Sketch009 [N_Axis]
  Refine = true
  Suppressed = false
  Type = 0
FEATURE [PartDesign::CoordinateSystem] FanHolder
  AttacherType = Attacher::AttachEngine3D
  AttachmentOffset = pos=(0,0,3) rot=(0,0,1;0rad)
  AttachmentSupport = -> [Pad007]
  MapMode = 11
  Placement = pos=(-35.75,35.75,4.5) rot=(0,0,1;1.5708rad)
FEATURE [Sketcher::SketchObject] Sketch033
  ArcFitTolerance = 1e-06
  AttachmentSupport = -> [Pad007]
  ExternalGeometry = -> [Pad007]
  FullyConstrained = true
  MakeInternals = false
  MapMode = 5
  Placement = pos=(0,0,1.5) rot=(0,0,1;0rad)
  sketch-geometry (8):
    g0: Circle CenterX=35.75 CenterY=35.75 CenterZ=0 NormalX=0 NormalY=0 NormalZ=1 AngleXU=0 Radius=2.5
    g1: Circle CenterX=35.75 CenterY=35.75 CenterZ=0 NormalX=0 NormalY=0 NormalZ=1 AngleXU=0 Radius=3.64645
    g2: Circle CenterX=-35.75 CenterY=35.75 CenterZ=0 NormalX=0 NormalY=0 NormalZ=1 AngleXU=0 Radius=2.5
    g3: Circle CenterX=-35.75 CenterY=35.75 CenterZ=0 NormalX=0 NormalY=0 NormalZ=1 AngleXU=0 Radius=3.64645
    g4: Circle CenterX=-35.75 CenterY=-35.75 CenterZ=0 NormalX=0 NormalY=0 NormalZ=1 AngleXU=0 Radius=2.5
    g5: Circle CenterX=-35.75 CenterY=-35.75 CenterZ=0 NormalX=0 NormalY=0 NormalZ=1 AngleXU=0 Radius=3.64645
    g6: Circle CenterX=35.75 CenterY=-35.75 CenterZ=0 NormalX=0 NormalY=0 NormalZ=1 AngleXU=0 Radius=2.5
    g7: Circle CenterX=35.75 CenterY=-35.75 CenterZ=0 NormalX=0 NormalY=0 NormalZ=1 AngleXU=0 Radius=3.64645
  constraints (16):
    c: Coincident(g0,g-3)
    c: Coincident(g1,g0)
    c: Coincident(g2,g-6)
    c: Coincident(g3,g2)
    c: Coincident(g4,g-5)
    c: Coincident(g5,g4)
    c: Coincident(g6,g-4)
    c: Coincident(g7,g6)
    c: Equal(g6,g4)
    c: Equal(g4,g2)
    c: Equal(g2,g0)
    c: Equal(g0,g-4)
    c: Equal(g7,g1)
    c: Equal(g1,g3)
    c: Equal(g3,g5)
    c: Tangent(g7,g-7)
FEATURE [PartDesign::Pad] Pad017
  BaseFeature = -> Pad007
  Direction = (0,0,1)
  Length = 10
  Length2 = 10
  Profile = -> Sketch033
  ReferenceAxis = -> Sketch033 [N_Axis]
  Refine = true
  Suppressed = false
  Type = 3
  UpToFace = -> Pad007 [Face132]
FEATURE [PartDesign::Body] Body001  label="FilterHolder"
  AllowCompound = false
  Group = -> [Sketch006,Pad004,Sketch007,Pad005,LinearPattern002,Sketch008,Pad006,LinearPattern003,Sketch009,Pad007,FanHolder,Sketch033,Pad017]
  Origin = -> Origin002
  Tip = -> Pad017
COMPONENT P2 — recipe-attached ("Base", modeled in this document).
Construction recipe (the document's own serialized feature program — sketch geometry with constraints, then the solid features built on it; lengths are millimeters unless a unit is written):

FEATURE [Sketcher::SketchObject] Sketch023
  ArcFitTolerance = 1e-06
  AttachmentSupport = -> [XY_Plane003]
  FullyConstrained = true
  MakeInternals = false
  MapMode = 5
  sketch-geometry (10):
    g0: LineSegment StartX=-55 StartY=25 StartZ=0 EndX=-55 EndY=-25 EndZ=0
    g1: LineSegment StartX=-45 StartY=-35 StartZ=0 EndX=45 EndY=-35 EndZ=0
    g2: LineSegment StartX=55 StartY=-25 StartZ=0 EndX=55 EndY=25 EndZ=0
    g3: LineSegment StartX=45 StartY=35 StartZ=0 EndX=-45 EndY=35 EndZ=0
    g4: ArcOfCircle CenterX=-45 CenterY=25 CenterZ=0 NormalX=0 NormalY=0 NormalZ=1 AngleXU=0 Radius=10 StartAngle=1.5708 EndAngle=3.14159
    g5: ArcOfCircle CenterX=-45 CenterY=-25 CenterZ=0 NormalX=0 NormalY=0 NormalZ=1 AngleXU=0 Radius=10 StartAngle=3.14159 EndAngle=4.71239
    g6: ArcOfCircle CenterX=45 CenterY=-25 CenterZ=0 NormalX=0 NormalY=0 NormalZ=1 AngleXU=0 Radius=10 StartAngle=4.71239 EndAngle=6.28319
    g7: ArcOfCircle CenterX=45 CenterY=25 CenterZ=0 NormalX=0 NormalY=0 NormalZ=1 AngleXU=0 Radius=10 StartAngle=1e-16 EndAngle=1.5708
    g8: GeomPoint [constr] X=-55 Y=35 Z=0
    g9: GeomPoint [constr] X=55 Y=-35 Z=0
  constraints (22):
    c: Tangent(g0,g4) = -1.5708
    c: Tangent(g0,g5) = -1.5708
    c: Tangent(g1,g5) = -1.5708
    c: Tangent(g1,g6) = -1.5708
    c: Tangent(g2,g6) = -1.5708
    c: Tangent(g2,g7) = -1.5708
    c: Tangent(g3,g7) = -1.5708
    c: Tangent(g3,g4) = -1.5708
    c: Vertical(g2)
    c: Horizontal(g1)
    c: Equal(g4,g5)
    c: Equal(g5,g6)
    c: Equal(g6,g7)
    c: PointOnObject(g8,g0)
    c: PointOnObject(g8,g3)
    c: PointOnObject(g9,g1)
    c: PointOnObject(g9,g2)
    c: Symmetric(g3,g3,g-2)
    c: Symmetric(g0,g0,g-1)
    c: DistanceX(g0,g2) = 110
    c: DistanceY(g1,g3) = 70
    c: Radius(g7) = 10
FEATURE [PartDesign::Pad] Pad014
  Direction = (0,0,1)
  Length = 20
  Length2 = 10
  Profile = -> Sketch023
  ReferenceAxis = -> Sketch023 [N_Axis]
  Refine = true
  Suppressed = false
  Type = 0
FEATURE [Sketcher::SketchObject] Sketch024
  ArcFitTolerance = 1e-06
  AttachmentSupport = -> [XZ_Plane003]
  ExternalGeometry = -> [Pad014]
  FullyConstrained = true
  MakeInternals = false
  MapMode = 5
  Placement = pos=(0,0,0) rot=(1,0,0;1.5708rad)
  sketch-geometry (5):
    g0: LineSegment StartX=55 StartY=20 StartZ=0 EndX=45 EndY=20 EndZ=0
    g1: ArcOfCircle CenterX=45 CenterY=16 CenterZ=0 NormalX=0 NormalY=0 NormalZ=1 AngleXU=0 Radius=4 StartAngle=0.413862 EndAngle=1.5708
    g2: ArcOfCircle CenterX=47 CenterY=1.5 CenterZ=0 NormalX=0 NormalY=0 NormalZ=1 AngleXU=0 Radius=8 StartAngle=3e-16 EndAngle=0.413862
    g3: LineSegment StartX=54.3246 StartY=4.71719 StartZ=0 EndX=48.6623 EndY=17.6086 EndZ=0
    g4: LineSegment StartX=55 StartY=20 StartZ=0 EndX=55 EndY=1.5 EndZ=0
  constraints (12):
    c: Horizontal(g0)
    c: Tangent(g1,g0) = -1.5708
    c: Tangent(g3,g2) = -1.5708
    c: Tangent(g3,g1) = -1.5708
    c: Coincident(g0,g-3)
    c: Coincident(g4,g0)
    c: PointOnObject(g4,g-3)
    c: Tangent(g4,g2) = 1.5708
    c: DistanceY(g2) = 1.5
    c: DistanceX(g0,g0) = 10
    c: Radius(g2) = 8
    c: Radius(g1) = 4
FEATURE [PartDesign::SubtractivePipe] SubtractivePipe
  AuxilleryCurvelinear = true
  AuxillerySpineTangent = false
  BaseFeature = -> Pad014
  Binormal = (0,0,0)
  Mode = 0
  Profile = -> Sketch024
  Refine = true
  Spine = -> Pad014 [Edge16,Edge19,Edge22,Edge24,Edge4,Edge7,Edge10,Edge13]
  SpineTangent = false
  Suppressed = false
  Transformation = 0
  Transition = 0
FEATURE [Sketcher::SketchObject] Sketch025
  ArcFitTolerance = 1e-06
  AttachmentSupport = -> [YZ_Plane003]
  ExternalGeometry = -> [SubtractivePipe]
  FullyConstrained = true
  MakeInternals = false
  MapMode = 5
  Placement = pos=(0,0,0) rot=(0.57735,0.57735,0.57735;2.0944rad)
  sketch-geometry (7):
    g0: LineSegment StartX=-7.5 StartY=20 StartZ=0 EndX=7.5 EndY=20 EndZ=0
    g1: ArcOfCircle CenterX=7.5 CenterY=23 CenterZ=0 NormalX=0 NormalY=0 NormalZ=1 AngleXU=0 Radius=3 StartAngle=3.14159 EndAngle=4.71239
    g2: ArcOfCircle CenterX=-7.5 CenterY=23 CenterZ=0 NormalX=0 NormalY=0 NormalZ=1 AngleXU=0 Radius=3 StartAngle=4.71239 EndAngle=6.28319
    g3: ArcOfCircle CenterX=8.84e-14 CenterY=28 CenterZ=0 NormalX=0 NormalY=0 NormalZ=1 AngleXU=0 Radius=4.5 StartAngle=-6.7475e-12 EndAngle=3.14159
    g4: LineSegment StartX=4.5 StartY=23 StartZ=0 EndX=4.5 EndY=28 EndZ=0
    g5: LineSegment StartX=-4.5 StartY=23 StartZ=0 EndX=-4.5 EndY=28 EndZ=0
    g6: Circle CenterX=8.84e-14 CenterY=28 CenterZ=0 NormalX=0 NormalY=0 NormalZ=1 AngleXU=0 Radius=2.75
  constraints (16):
    c: PointOnObject(g0,g-3)
    c: Symmetric(g0,g0,g-2)
    c: Vertical(g5)
    c: Tangent(g4,g3) = -1.5708
    c: Tangent(g4,g1) = 1.5708
    c: Tangent(g1,g0) = -1.5708
    c: Tangent(g2,g0) = -1.5708
    c: Tangent(g5,g2) = -1.5708
    c: Tangent(g5,g3) = 1.5708
    c: Vertical(g4)
    c: Equal(g1,g2)
    c: Diameter(g3) = 9
    c: Coincident(g6,g3)
    c: Diameter(g6) = 5.5
    c: Radius(g1) = 3
    c: DistanceY(g0,g3) = 8
FEATURE [PartDesign::Pad] Pad015
  BaseFeature = -> SubtractivePipe
  Direction = (1,0,0)
  Length = 70
  Length2 = 10
  Midplane = true
  Profile = -> Sketch025
  ReferenceAxis = -> Sketch025 [N_Axis]
  Refine = true
  Suppressed = false
  Type = 0
FEATURE [Sketcher::SketchObject] Sketch026
  ArcFitTolerance = 1e-06
  AttachmentSupport = -> [XZ_Plane003]
  ExternalGeometry = -> [Pad015]
  FullyConstrained = true
  MakeInternals = false
  MapMode = 5
  Placement = pos=(0,0,0) rot=(1,0,0;1.5708rad)
  sketch-geometry (5):
    g0: LineSegment StartX=-25.5 StartY=35 StartZ=0 EndX=-25.5 EndY=20 EndZ=0
    g1: LineSegment StartX=-25.5 StartY=20 StartZ=0 EndX=25.5 EndY=20 EndZ=0
    g2: LineSegment StartX=25.5 StartY=20 StartZ=0 EndX=25.5 EndY=35 EndZ=0
    g3: LineSegment StartX=25.5 StartY=35 StartZ=0 EndX=-25.5 EndY=35 EndZ=0
    g4: GeomPoint [constr] X=0 Y=27.5 Z=0
  constraints (13):
    c: Coincident(g0,g1)
    c: Coincident(g1,g2)
    c: Coincident(g2,g3)
    c: Coincident(g3,g0)
    c: Vertical(g0)
    c: Vertical(g2)
    c: Horizontal(g1)
    c: Horizontal(g3)
    c: Symmetric(g2,g0,g4)
    c: PointOnObject(g4,g-2)
    c: PointOnObject(g1,g-3)
    c: DistanceX(g3,g3) = 51
    c: DistanceY(g2,g2) = 15
FEATURE [PartDesign::Pocket] Pocket004
  BaseFeature = -> Pad015
  Direction = (0,1,-2e-16)
  Length = 5
  Length2 = 5
  Midplane = true
  Profile = -> Sketch026
  ReferenceAxis = -> Sketch026 [N_Axis]
  Refine = true
  Suppressed = false
  Type = 1
FEATURE [Sketcher::SketchObject] Sketch027
  ArcFitTolerance = 1e-06
  AttachmentSupport = -> [Pocket004]
  ExternalGeometry = -> [Pocket004]
  FullyConstrained = true
  MakeInternals = false
  MapMode = 5
  Placement = pos=(0,-30.5104,13.4011) rot=(1,0,0;1.15693rad)
  sketch-geometry (5):
    g0: LineSegment StartX=-34.25 StartY=0 StartZ=0 EndX=-34.25 EndY=-4 EndZ=0
    g1: LineSegment StartX=-34.25 StartY=-4 StartZ=0 EndX=-26.25 EndY=-4 EndZ=0
    g2: LineSegment StartX=-26.25 StartY=-4 StartZ=0 EndX=-26.25 EndY=0 EndZ=0
    g3: LineSegment StartX=-26.25 StartY=0 StartZ=0 EndX=-34.25 EndY=0 EndZ=0
    g4: LineSegment [constr] StartX=-30.25 StartY=0 StartZ=0 EndX=-30.25 EndY=15.2954 EndZ=0
  constraints (14):
    c: Coincident(g0,g1)
    c: Coincident(g1,g2)
    c: Coincident(g2,g3)
    c: Coincident(g3,g0)
    c: Vertical(g0)
    c: Vertical(g2)
    c: Horizontal(g1)
    c: Horizontal(g3)
    c: PointOnObject(g0,g-1)
    c: DistanceY(g2,g2) = 4
    c: DistanceX(g1,g1) = 8
    c: Symmetric(g3,g3,g4)
    c: Vertical(g4)
    c: Symmetric(g-3,g-3,g4)
FEATURE [PartDesign::Pocket] Pocket005
  BaseFeature = -> Pocket004
  Direction = (0,0.915575,-0.402148)
  Length = 10
  Length2 = 5
  Profile = -> Sketch027
  ReferenceAxis = -> Sketch027 [N_Axis]
  Refine = true
  Suppressed = false
  Type = 0
FEATURE [Sketcher::SketchObject] Sketch028
  ArcFitTolerance = 1e-06
  AttachmentSupport = -> [Pocket005]
  ExternalGeometry = -> [Pocket005]
  FullyConstrained = true
  MakeInternals = false
  MapMode = 5
  Placement = pos=(-2.8e-15,35,0) rot=(0,0.707107,0.707107;3.14159rad)
  sketch-geometry (6):
    g0: LineSegment StartX=24.25 StartY=15.1629 StartZ=0 EndX=24.25 EndY=7.16289 EndZ=0
    g1: LineSegment StartX=24.25 StartY=7.16289 StartZ=0 EndX=36.25 EndY=7.16289 EndZ=0
    g2: LineSegment StartX=36.25 StartY=7.16289 StartZ=0 EndX=36.25 EndY=15.1629 EndZ=0
    g3: LineSegment StartX=36.25 StartY=15.1629 StartZ=0 EndX=24.25 EndY=15.1629 EndZ=0
    g4: LineSegment [constr] StartX=30.25 StartY=15.1629 StartZ=0 EndX=30.25 EndY=23 EndZ=0
    g5: LineSegment [constr] StartX=45 StartY=11.1629 StartZ=0 EndX=36.25 EndY=11.1629 EndZ=0
  constraints (16):
    c: Coincident(g0,g1)
    c: Coincident(g1,g2)
    c: Coincident(g2,g3)
    c: Coincident(g3,g0)
    c: Vertical(g0)
    c: Vertical(g2)
    c: Horizontal(g1)
    c: Horizontal(g3)
    c: Symmetric(g3,g3,g4)
    c: Symmetric(g-3,g-3,g4)
    c: Vertical(g4)
    c: DistanceX(g3,g3) = 12
    c: DistanceY(g2,g2) = 8
    c: Symmetric(g-4,g-4,g5)
    c: Symmetric(g2,g2,g5)
    c: Horizontal(g5)
FEATURE [PartDesign::Pocket] Pocket006
  BaseFeature = -> Pocket005
  Direction = (0,-1,2e-16)
  Length = 63
  Length2 = 5
  Profile = -> Sketch028
  ReferenceAxis = -> Sketch028 [N_Axis]
  Refine = true
  Suppressed = false
  Type = 0
FEATURE [Sketcher::SketchObject] Sketch029
  ArcFitTolerance = 1e-06
  AttachmentSupport = -> [Pocket006]
  ExternalGeometry = -> [Pocket006]
  FullyConstrained = true
  MakeInternals = false
  MapMode = 5
  Placement = pos=(0,0,0) rot=(1,0,0;3.14159rad)
  sketch-geometry (10):
    g0: LineSegment StartX=-45 StartY=20 StartZ=0 EndX=-45 EndY=-20 EndZ=0
    g1: LineSegment StartX=-40 StartY=-25 StartZ=0 EndX=40 EndY=-25 EndZ=0
    g2: LineSegment StartX=45 StartY=-20 StartZ=0 EndX=45 EndY=20 EndZ=0
    g3: LineSegment StartX=40 StartY=25 StartZ=0 EndX=-40 EndY=25 EndZ=0
    g4: ArcOfCircle CenterX=-40 CenterY=20 CenterZ=0 NormalX=0 NormalY=0 NormalZ=1 AngleXU=0 Radius=5 StartAngle=1.5708 EndAngle=3.14159
    g5: ArcOfCircle CenterX=-40 CenterY=-20 CenterZ=0 NormalX=0 NormalY=0 NormalZ=1 AngleXU=0 Radius=5 StartAngle=3.14159 EndAngle=4.71239
    g6: ArcOfCircle CenterX=40 CenterY=-20 CenterZ=0 NormalX=0 NormalY=0 NormalZ=1 AngleXU=0 Radius=5 StartAngle=4.71239 EndAngle=6.28319
    g7: ArcOfCircle CenterX=40 CenterY=20 CenterZ=0 NormalX=0 NormalY=0 NormalZ=1 AngleXU=0 Radius=5 StartAngle=9.685e-13 EndAngle=1.5708
    g8: GeomPoint [constr] X=-45 Y=25 Z=0
    g9: GeomPoint [constr] X=45 Y=-25 Z=0
  constraints (22):
    c: Tangent(g0,g4) = -1.5708
    c: Tangent(g0,g5) = -1.5708
    c: Tangent(g1,g5) = -1.5708
    c: Tangent(g1,g6) = -1.5708
    c: Tangent(g2,g6) = -1.5708
    c: Tangent(g2,g7) = -1.5708
    c: Tangent(g3,g7) = -1.5708
    c: Tangent(g3,g4) = -1.5708
    c: Vertical(g2)
    c: Horizontal(g1)
    c: Equal(g4,g5)
    c: Equal(g5,g6)
    c: Equal(g6,g7)
    c: PointOnObject(g8,g0)
    c: PointOnObject(g8,g3)
    c: PointOnObject(g9,g1)
    c: PointOnObject(g9,g2)
    c: Radius(g5) = 5
    c: Symmetric(g3,g3,g-2)
    c: Symmetric(g0,g0,g-1)
    c: DistanceX(g2,g-3) = 10
    c: DistanceY(g3,g-4) = 10
FEATURE [PartDesign::Pocket] Pocket007
  BaseFeature = -> Pocket006
  Direction = (0,0,1)
  Length = 15
  Length2 = 5
  Profile = -> Sketch029
  ReferenceAxis = -> Sketch029 [N_Axis]
  Refine = true
  Suppressed = false
  Type = 0
FEATURE [PartDesign::CoordinateSystem] Fan  label="FanHolders"
  AttacherType = Attacher::AttachEngine3D
  AttachmentSupport = -> [Pocket007]
  MapMode = 45
  Placement = pos=(0,1.014e-13,28) rot=(0.57735,0.57735,0.57735;2.0944rad)
FEATURE [PartDesign::CoordinateSystem] Bottom
  AttacherType = Attacher::AttachEngine3D
  AttachmentSupport = -> [Pocket007]
  MapMode = 45
  Placement = pos=(-2.3879e-12,-1.227e-13,0) rot=(0,0,1;1.5708rad)
FEATURE [PartDesign::Body] Body002  label="Base"
  AllowCompound = false
  Group = -> [Sketch023,Pad014,Sketch024,SubtractivePipe,Sketch025,Pad015,Sketch026,Pocket004,Sketch027,Pocket005,Sketch028,Pocket006,Sketch029,Pocket007,Fan,Bottom]
  Origin = -> Origin003
  Tip = -> Pocket007
COMPONENT P3 — recipe-attached ("Fan2Holder", modeled in this document).
Construction recipe (the document's own serialized feature program — sketch geometry with constraints, then the solid features built on it; lengths are millimeters unless a unit is written):

FEATURE [Sketcher::SketchObject] Sketch014
  ArcFitTolerance = 1e-06
  AttachmentSupport = -> [XY_Plane004]
  FullyConstrained = true
  MakeInternals = false
  MapMode = 5
  sketch-geometry (13):
    g0: LineSegment StartX=-42.5 StartY=35.75 StartZ=0 EndX=-42.5 EndY=-35.75 EndZ=0
    g1: LineSegment StartX=-35.75 StartY=-42.5 StartZ=0 EndX=60 EndY=-42.5 EndZ=0
    g2: LineSegment StartX=60 StartY=-42.5 StartZ=0 EndX=60 EndY=42.5 EndZ=0
    g3: LineSegment StartX=60 StartY=42.5 StartZ=0 EndX=-35.75 EndY=42.5 EndZ=0
    g4: Circle CenterX=-35.75 CenterY=35.75 CenterZ=0 NormalX=0 NormalY=0 NormalZ=1 AngleXU=0 Radius=2.5
    g5: Circle CenterX=35.75 CenterY=35.75 CenterZ=0 NormalX=0 NormalY=0 NormalZ=1 AngleXU=0 Radius=2.5
    g6: Circle CenterX=-35.75 CenterY=-35.75 CenterZ=0 NormalX=0 NormalY=0 NormalZ=1 AngleXU=0 Radius=2.5
    g7: Circle CenterX=35.75 CenterY=-35.75 CenterZ=0 NormalX=0 NormalY=0 NormalZ=1 AngleXU=0 Radius=2.5
    g8: Circle CenterX=0 CenterY=0 CenterZ=0 NormalX=0 NormalY=0 NormalZ=1 AngleXU=0 Radius=38.75
    g9: ArcOfCircle CenterX=-35.75 CenterY=35.75 CenterZ=0 NormalX=0 NormalY=0 NormalZ=1 AngleXU=0 Radius=6.75 StartAngle=1.5708 EndAngle=3.14159
    g10: GeomPoint [constr] X=-42.5 Y=42.5 Z=0
    g11: ArcOfCircle CenterX=-35.75 CenterY=-35.75 CenterZ=0 NormalX=0 NormalY=0 NormalZ=1 AngleXU=0 Radius=6.75 StartAngle=3.14159 EndAngle=4.71239
    g12: GeomPoint [constr] X=-42.5 Y=-42.5 Z=0
  constraints (30):
    c: Coincident(g1,g2)
    c: Coincident(g2,g3)
    c: Vertical(g2)
    c: Horizontal(g1)
    c: Horizontal(g3)
    c: DistanceY(g12,g10) = 85
    c: Equal(g7,g5)
    c: Equal(g5,g4)
    c: Equal(g4,g6)
    c: Diameter(g7) = 5
    c: Symmetric(g7,g5,g-1)
    c: Symmetric(g5,g4,g-2)
    c: Vertical(g6,g4)
    c: Horizontal(g6,g7)
    c: DistanceX(g4,g5) = 71.5
    c: DistanceY(g6,g4) = 71.5
    c: Symmetric(g12,g10,g-1)
    c: Coincident(g8,g-1)
    c: Diameter(g8) = 77.5
    c: DistanceX(g10,g-1) = 42.5
    c: DistanceX(g1) = 60
    c: PointOnObject(g10,g0)
    c: PointOnObject(g10,g3)
    c: Tangent(g0,g9) = -1.5708
    c: Tangent(g3,g9) = -1.5708
    c: PointOnObject(g12,g1)
    c: Tangent(g0,g11) = -1.5708
    c: Tangent(g1,g11) = -1.5708
    c: Equal(g11,g9)
    c: Coincident(g9,g4)
FEATURE [PartDesign::Pad] Pad010
  Direction = (0,0,1)
  Length = 1.5
  Length2 = 10
  Profile = -> Sketch014
  ReferenceAxis = -> Sketch014 [N_Axis]
  Refine = true
  Suppressed = false
  Type = 0
FEATURE [Sketcher::SketchObject] Sketch015
  ArcFitTolerance = 1e-06
  AttachmentSupport = -> [Pad010]
  ExternalGeometry = -> [Pad010]
  FullyConstrained = true
  MakeInternals = false
  MapMode = 5
  Placement = pos=(0,0,1.5) rot=(0,0,1;0rad)
  sketch-geometry (12):
    g0: LineSegment StartX=60 StartY=42.5 StartZ=0 EndX=-35.75 EndY=42.5 EndZ=0
    g1: LineSegment StartX=-42.5 StartY=35.75 StartZ=0 EndX=-42.5 EndY=-35.75 EndZ=0
    g2: LineSegment StartX=-35.75 StartY=-42.5 StartZ=0 EndX=60 EndY=-42.5 EndZ=0
    g3: ArcOfCircle CenterX=-35.75 CenterY=-35.75 CenterZ=0 NormalX=0 NormalY=0 NormalZ=1 AngleXU=0 Radius=6.75 StartAngle=3.14159 EndAngle=4.71239
    g4: ArcOfCircle CenterX=-35.75 CenterY=35.75 CenterZ=0 NormalX=0 NormalY=0 NormalZ=1 AngleXU=0 Radius=6.75 StartAngle=1.5708 EndAngle=3.14159
    g5: LineSegment StartX=60 StartY=-42.5 StartZ=0 EndX=60 EndY=-41 EndZ=0
    g6: LineSegment StartX=60 StartY=-41 StartZ=0 EndX=-35.75 EndY=-41 EndZ=0
    g7: LineSegment StartX=-41 StartY=-35.75 StartZ=0 EndX=-41 EndY=35.75 EndZ=0
    g8: LineSegment StartX=-35.75 StartY=41 StartZ=0 EndX=60 EndY=41 EndZ=0
    g9: LineSegment StartX=60 StartY=41 StartZ=0 EndX=60 EndY=42.5 EndZ=0
    g10: ArcOfCircle CenterX=-35.75 CenterY=-35.75 CenterZ=0 NormalX=0 NormalY=0 NormalZ=1 AngleXU=0 Radius=5.25 StartAngle=3.14159 EndAngle=4.71239
    g11: ArcOfCircle CenterX=-35.75 CenterY=35.75 CenterZ=0 NormalX=0 NormalY=0 NormalZ=1 AngleXU=0 Radius=5.25 StartAngle=1.5708 EndAngle=3.14159
  constraints (30):
    c: Coincident(g0,g-3)
    c: Coincident(g0,g-4)
    c: Horizontal(g2)
    c: Symmetric(g2,g0,g-1)
    c: Equal(g2,g0)
    c: Coincident(g-5,g1)
    c: Coincident(g1,g-5)
    c: Coincident(g3,g2)
    c: Coincident(g3,g1)
    c: Coincident(g4,g1)
    c: Coincident(g4,g0)
    c: Equal(g4,g-4)
    c: Equal(g-4,g3)
    c: Coincident(g5,g2)
    c: Vertical(g5)
    c: Coincident(g6,g5)
    c: Horizontal(g6)
    c: Vertical(g7)
    c: Coincident(g9,g8)
    c: Coincident(g9,g0)
    c: Horizontal(g8)
    c: Vertical(g9)
    c: Equal(g5,g9)
    c: Equal(g6,g8)
    c: Tangent(g10,g6) = 1.5708
    c: Tangent(g10,g7) = 1.5708
    c: Tangent(g11,g7) = 1.5708
    c: Tangent(g11,g8) = 1.5708
    c: DistanceY(g5,g5) = 1.5
    c: Coincident(g11,g4)
FEATURE [PartDesign::Pad] Pad011
  BaseFeature = -> Pad010
  Direction = (0,0,1)
  Length = 5
  Length2 = 10
  Profile = -> Sketch015
  ReferenceAxis = -> Sketch015 [N_Axis]
  Refine = true
  Suppressed = false
  Type = 0
FEATURE [Sketcher::SketchObject] Sketch016
  ArcFitTolerance = 1e-06
  AttachmentSupport = -> [Pad011]
  ExternalGeometry = -> [Pad011]
  FullyConstrained = true
  MakeInternals = false
  MapMode = 5
  Placement = pos=(60,0,0) rot=(0.57735,0.57735,0.57735;2.0944rad)
  sketch-geometry (9):
    g0: LineSegment StartX=41.1112 StartY=6.9583 StartZ=0 EndX=45 EndY=14.5 EndZ=0
    g1: LineSegment [constr] StartX=45 StartY=14.5 StartZ=0 EndX=46.5 EndY=14.5 EndZ=0
    g2: LineSegment StartX=46.5 StartY=14.5 StartZ=0 EndX=42.6112 EndY=6.9583 EndZ=0
    g3: ArcOfCircle CenterX=43.5 CenterY=6.5 CenterZ=0 NormalX=0 NormalY=0 NormalZ=1 AngleXU=0 Radius=1 StartAngle=2.66551 EndAngle=3.14159
    g4: ArcOfCircle CenterX=42 CenterY=6.5 CenterZ=0 NormalX=0 NormalY=0 NormalZ=1 AngleXU=0 Radius=1 StartAngle=2.66551 EndAngle=3.14159
    g5: LineSegment StartX=42.5 StartY=6.5 StartZ=0 EndX=41 EndY=6.5 EndZ=0
    g6: LineSegment StartX=45 StartY=14.5 StartZ=0 EndX=45 EndY=29.5 EndZ=0
    g7: LineSegment StartX=45 StartY=29.5 StartZ=0 EndX=46.5 EndY=29.5 EndZ=0
    g8: LineSegment StartX=46.5 StartY=29.5 StartZ=0 EndX=46.5 EndY=14.5 EndZ=0
  constraints (24):
    c: Coincident(g0,g1)
    c: Horizontal(g1)
    c: Coincident(g1,g2)
    c: Coincident(g3,g-3)
    c: Coincident(g4,g-3)
    c: Tangent(g4,g0) = 1.5708
    c: Tangent(g3,g2) = -1.5708
    c: Coincident(g5,g3)
    c: Coincident(g5,g4)
    c: Perpendicular(g3,g5)
    c: Perpendicular(g4,g5)
    c: Equal(g1,g5)
    c: Radius(g4) = 1
    c: DistanceY(g3,g1) = 8
    c: DistanceX(g3,g1) = 4
    c: Equal(g4,g3)
    c: Coincident(g0,g6)
    c: Vertical(g6)
    c: Coincident(g6,g7)
    c: Horizontal(g7)
    c: Coincident(g7,g8)
    c: Coincident(g8,g1)
    c: Vertical(g8)
    c: DistanceY(g8,g8) = 15
FEATURE [PartDesign::AdditivePipe] AdditivePipe001
  AuxilleryCurvelinear = true
  AuxillerySpineTangent = false
  BaseFeature = -> Pad011
  Binormal = (0,0,0)
  Mode = 0
  Profile = -> Sketch016
  Refine = true
  Spine = -> Pad011 [Edge32,Edge33,Edge34,Edge35,Edge36]
  SpineTangent = false
  Suppressed = false
  Transformation = 0
  Transition = 0
FEATURE [Sketcher::SketchObject] Sketch017
  ArcFitTolerance = 1e-06
  AttachmentSupport = -> [XY_Plane004]
  ExternalGeometry = -> [AdditivePipe001]
  FullyConstrained = true
  MakeInternals = false
  MapMode = 5
  sketch-geometry (5):
    g0: LineSegment StartX=-30.75 StartY=42.5 StartZ=0 EndX=-30.75 EndY=-42.5 EndZ=0
    g1: LineSegment StartX=-30.75 StartY=-42.5 StartZ=0 EndX=-29.25 EndY=-42.5 EndZ=0
    g2: LineSegment StartX=-29.25 StartY=-42.5 StartZ=0 EndX=-29.25 EndY=42.5 EndZ=0
    g3: LineSegment StartX=-29.25 StartY=42.5 StartZ=0 EndX=-30.75 EndY=42.5 EndZ=0
    g4: GeomPoint [constr] X=-30 Y=0 Z=0
  constraints (13):
    c: Coincident(g0,g1)
    c: Coincident(g1,g2)
    c: Coincident(g2,g3)
    c: Coincident(g3,g0)
    c: Vertical(g0)
    c: Vertical(g2)
    c: Horizontal(g1)
    c: Horizontal(g3)
    c: Symmetric(g2,g0,g4)
    c: PointOnObject(g4,g-1)
    c: PointOnObject(g1,g-3)
    c: DistanceX(g3,g3) = 1.5
    c: DistanceX(g4,g-1) = 30
FEATURE [PartDesign::Pad] Pad012
  BaseFeature = -> AdditivePipe001
  Direction = (0,0,1)
  Length = 10
  Length2 = 10
  Profile = -> Sketch017
  ReferenceAxis = -> Sketch017 [N_Axis]
  Refine = true
  Suppressed = false
  Type = 3
  UpToFace = -> AdditivePipe001 [Face4]
FEATURE [PartDesign::LinearPattern] LinearPattern004
  BaseFeature = -> Pad012
  Direction = -> Sketch017 [H_Axis]
  Length = 60
  Mode = 0
  Occurrences = 5
  Offset = 15
  Originals = -> [Pad012]
  Refine = true
  Suppressed = false
  TransformMode = 0
FEATURE [Sketcher::SketchObject] Sketch018
  ArcFitTolerance = 1e-06
  AttachmentSupport = -> [XY_Plane004]
  ExternalGeometry = -> [LinearPattern004]
  FullyConstrained = true
  MakeInternals = false
  MapMode = 5
  sketch-geometry (5):
    g0: LineSegment StartX=42.5 StartY=29.25 StartZ=0 EndX=42.5 EndY=30.75 EndZ=0
    g1: LineSegment StartX=42.5 StartY=30.75 StartZ=0 EndX=-42.5 EndY=30.75 EndZ=0
    g2: LineSegment StartX=-42.5 StartY=30.75 StartZ=0 EndX=-42.5 EndY=29.25 EndZ=0
    g3: LineSegment StartX=-42.5 StartY=29.25 StartZ=0 EndX=42.5 EndY=29.25 EndZ=0
    g4: GeomPoint [constr] X=0 Y=30 Z=0
  constraints (13):
    c: Coincident(g0,g1)
    c: Coincident(g1,g2)
    c: Coincident(g2,g3)
    c: Coincident(g3,g0)
    c: Vertical(g0)
    c: Vertical(g2)
    c: Horizontal(g1)
    c: Horizontal(g3)
    c: Symmetric(g2,g0,g4)
    c: PointOnObject(g4,g-2)
    c: PointOnObject(g1,g-3)
    c: DistanceY(g4) = 30
    c: DistanceY(g0,g0) = 1.5
FEATURE [PartDesign::Pad] Pad013
  BaseFeature = -> LinearPattern004
  Direction = (0,0,1)
  Length = 10
  Length2 = 10
  Profile = -> Sketch018
  ReferenceAxis = -> Sketch018 [N_Axis]
  Refine = true
  Suppressed = false
  Type = 3
  UpToFace = -> LinearPattern004 [Face68]
FEATURE [PartDesign::LinearPattern] LinearPattern005
  BaseFeature = -> Pad013
  Direction = -> Sketch018 [V_Axis]
  Length = 60
  Mode = 0
  Occurrences = 5
  Offset = 15
  Originals = -> [Pad013]
  Refine = true
  Reversed = true
  Suppressed = false
  TransformMode = 0
FEATURE [PartDesign::CoordinateSystem] FanMountHole001
  AttacherType = Attacher::AttachEngine3D
  AttachmentSupport = -> [LinearPattern005]
  MapMode = 11
  Placement = pos=(-35.75,-35.75,0) rot=(0,0,1;1.5708rad)
FEATURE [Sketcher::SketchObject] Sketch019
  ArcFitTolerance = 1e-06
  AttachmentSupport = -> [XZ_Plane004]
  ExternalGeometry = -> [LinearPattern005]
  FullyConstrained = true
  MakeInternals = false
  MapMode = 5
  Placement = pos=(0,0,0) rot=(1,0,0;1.5708rad)
  sketch-geometry (4):
    g0: LineSegment StartX=60 StartY=29.5 StartZ=0 EndX=60 EndY=0 EndZ=0
    g1: LineSegment StartX=60 StartY=0 StartZ=0 EndX=43 EndY=0 EndZ=0
    g2: LineSegment StartX=43 StartY=0 StartZ=0 EndX=37.7984 EndY=29.5 EndZ=0
    g3: LineSegment StartX=37.7984 StartY=29.5 StartZ=0 EndX=60 EndY=29.5 EndZ=0
  constraints (11):
    c: PointOnObject(g0,g-1)
    c: Vertical(g0)
    c: Coincident(g0,g1)
    c: PointOnObject(g1,g-1)
    c: Coincident(g1,g2)
    c: Coincident(g2,g3)
    c: Coincident(g3,g0)
    c: DistanceX(g-1,g1) = 43
    c: Angle(g1,g2) = 1.74533
    c: Coincident(g0,g-3)
    c: PointOnObject(g2,g-3)
FEATURE [PartDesign::Pocket] Pocket002
  BaseFeature = -> LinearPattern005
  Direction = (0,1,-2e-16)
  Length = 5
  Length2 = 5
  Midplane = true
  Profile = -> Sketch019
  ReferenceAxis = -> Sketch019 [N_Axis]
  Refine = true
  Suppressed = false
  Type = 1
FEATURE [PartDesign::CoordinateSystem] FilterHolderMount001
  AttacherType = Attacher::AttachEngine3D
  AttachmentSupport = -> [Pocket002]
  MapMode = 11
  Placement = pos=(-35.75,35.75,1.5) rot=(0,0,1;1.5708rad)
FEATURE [PartDesign::CoordinateSystem] OtherFanHolder001
  AttacherType = Attacher::AttachEngine3D
  AttachmentSupport = -> [Pocket002]
  MapMode = 45
  Placement = pos=(42.8701,0,0.736527) rot=(0.642788,0,0.766044;3.14159rad)
FEATURE [Sketcher::SketchObject] Sketch022
  ArcFitTolerance = 1e-06
  FullyConstrained = true
  MakeInternals = false
  MapMode = 5
  Placement = pos=(41.7034,1.6e-15,7.35343) rot=(0.540716,0.540716,0.6444;1.99673rad)
  sketch-geometry (6):
    g0: ArcOfCircle CenterX=43.0908 CenterY=-0.761797 CenterZ=0 NormalX=0 NormalY=0 NormalZ=1 AngleXU=0 Radius=0.6 StartAngle=2.49691 EndAngle=3.31716
    g1: LineSegment StartX=44.66 StartY=3.6334 StartZ=0 EndX=42.6112 EndY=-0.401229 EndZ=0
    g2: LineSegment StartX=42.5 StartY=-5.3666 StartZ=0 EndX=42.5 EndY=-0.866599 EndZ=0
    g3: LineSegment StartX=42.5 StartY=-5.3666 StartZ=0 EndX=50.5 EndY=-5.3666 EndZ=0
    g4: LineSegment StartX=44.66 StartY=3.6334 StartZ=0 EndX=50.5 EndY=3.6334 EndZ=0
    g5: ArcOfCircle CenterX=50.5 CenterY=-0.866599 CenterZ=0 NormalX=0 NormalY=0 NormalZ=1 AngleXU=0 Radius=4.5 StartAngle=4.71239 EndAngle=7.85398
  constraints (16):
    c: Coincident(g0,g-3)
    c: Coincident(g0,g-4)
    c: Radius(g0) = 0.6
    c: Coincident(g3,g2)
    c: Horizontal(g3)
    c: Coincident(g4,g1)
    c: Horizontal(g4)
    c: Diameter(g5) = 9
    c: PointOnObject(g1,g-4)
    c: Horizontal(g5,g2)
    c: Tangent(g5,g3) = -1.5708
    c: Tangent(g5,g4) = 1.5708
    c: DistanceX(g-4,g5) = 4
    c: Coincident(g2,g0)
    c: Coincident(g0,g1)
    c: PointOnObject(g2,g-3)
FEATURE [PartDesign::Pocket] Pocket003
  BaseFeature = -> Pocket002
  Direction = (-0.984808,2e-16,-0.173648)
  Length = 50
  Length2 = 5
  Midplane = true
  Profile = -> Sketch022
  ReferenceAxis = -> Sketch022 [N_Axis]
  Refine = true
  Suppressed = false
  Type = 0
FEATURE [PartDesign::Body] Body003  label="Fan2Holder"
  AllowCompound = false
  Group = -> [Sketch014,Pad010,Sketch015,Pad011,Sketch016,AdditivePipe001,Sketch017,Pad012,LinearPattern004,Sketch018,Pad013,LinearPattern005,FanMountHole001,Sketch019,Pocket002,OtherFanHolder001,FilterHolderMount001,Sketch022,Pocket003]
  Origin = -> Origin004
  Tip = -> Pocket003
COMPONENT P4 — recipe-attached ("BottomCover", modeled in this document).
Construction recipe (the document's own serialized feature program — sketch geometry with constraints, then the solid features built on it; lengths are millimeters unless a unit is written):

FEATURE [Sketcher::SketchObject] Sketch030
  ArcFitTolerance = 1e-06
  AttachmentSupport = -> [XY_Plane005]
  FullyConstrained = true
  MakeInternals = false
  MapMode = 5
  sketch-geometry (10):
    g0: LineSegment StartX=-55 StartY=25 StartZ=0 EndX=-55 EndY=-25 EndZ=0
    g1: LineSegment StartX=-45 StartY=-35 StartZ=0 EndX=45 EndY=-35 EndZ=0
    g2: LineSegment StartX=55 StartY=-25 StartZ=0 EndX=55 EndY=25 EndZ=0
    g3: LineSegment StartX=45 StartY=35 StartZ=0 EndX=-45 EndY=35 EndZ=0
    g4: ArcOfCircle CenterX=-45 CenterY=25 CenterZ=0 NormalX=0 NormalY=0 NormalZ=1 AngleXU=0 Radius=10 StartAngle=1.5708 EndAngle=3.14159
    g5: ArcOfCircle CenterX=-45 CenterY=-25 CenterZ=0 NormalX=0 NormalY=0 NormalZ=1 AngleXU=0 Radius=10 StartAngle=3.14159 EndAngle=4.71239
    g6: ArcOfCircle CenterX=45 CenterY=-25 CenterZ=0 NormalX=0 NormalY=0 NormalZ=1 AngleXU=0 Radius=10 StartAngle=4.71239 EndAngle=6.28319
    g7: ArcOfCircle CenterX=45 CenterY=25 CenterZ=0 NormalX=0 NormalY=0 NormalZ=1 AngleXU=0 Radius=10 StartAngle=0 EndAngle=1.5708
    g8: GeomPoint [constr] X=-55 Y=35 Z=0
    g9: GeomPoint [constr] X=55 Y=-35 Z=0
  constraints (22):
    c: Tangent(g0,g4) = -1.5708
    c: Tangent(g0,g5) = -1.5708
    c: Tangent(g1,g5) = -1.5708
    c: Tangent(g1,g6) = -1.5708
    c: Tangent(g2,g6) = -1.5708
    c: Tangent(g2,g7) = -1.5708
    c: Tangent(g3,g7) = -1.5708
    c: Tangent(g3,g4) = -1.5708
    c: Vertical(g2)
    c: Horizontal(g1)
    c: Equal(g4,g5)
    c: Equal(g5,g6)
    c: Equal(g6,g7)
    c: PointOnObject(g8,g0)
    c: PointOnObject(g8,g3)
    c: PointOnObject(g9,g1)
    c: PointOnObject(g9,g2)
    c: Radius(g5) = 10
    c: Symmetric(g3,g3,g-2)
    c: Symmetric(g0,g0,g-1)
    c: DistanceX(g0,g2) = 110
    c: DistanceY(g1,g3) = 70
FEATURE [PartDesign::Pad] Pad016
  Direction = (0,0,1)
  Length = 1.5
  Length2 = 10
  Profile = -> Sketch030
  ReferenceAxis = -> Sketch030 [N_Axis]
  Refine = true
  Suppressed = false
  Type = 0
FEATURE [PartDesign::CoordinateSystem] Base001  label="Base002"
  AttacherType = Attacher::AttachEngine3D
  AttachmentSupport = -> [Pad016]
  MapMode = 45
  Placement = pos=(-8.91e-14,-6.93e-14,1.5) rot=(0,0,1;1.5708rad)
FEATURE [PartDesign::Body] Body004  label="BottomCover"
  AllowCompound = false
  Group = -> [Sketch030,Base001,Pad016]
  Origin = -> Origin005
  Tip = -> Pad016
PROVENANCE & LICENSES
A FreeCAD (.FCStd) document from a public repository crawl; recipes are the document's own serialized feature recipes (and, for linked parts, companion documents' recipes).
License: as declared in the source repository (recorded in the dataset sidecar).
